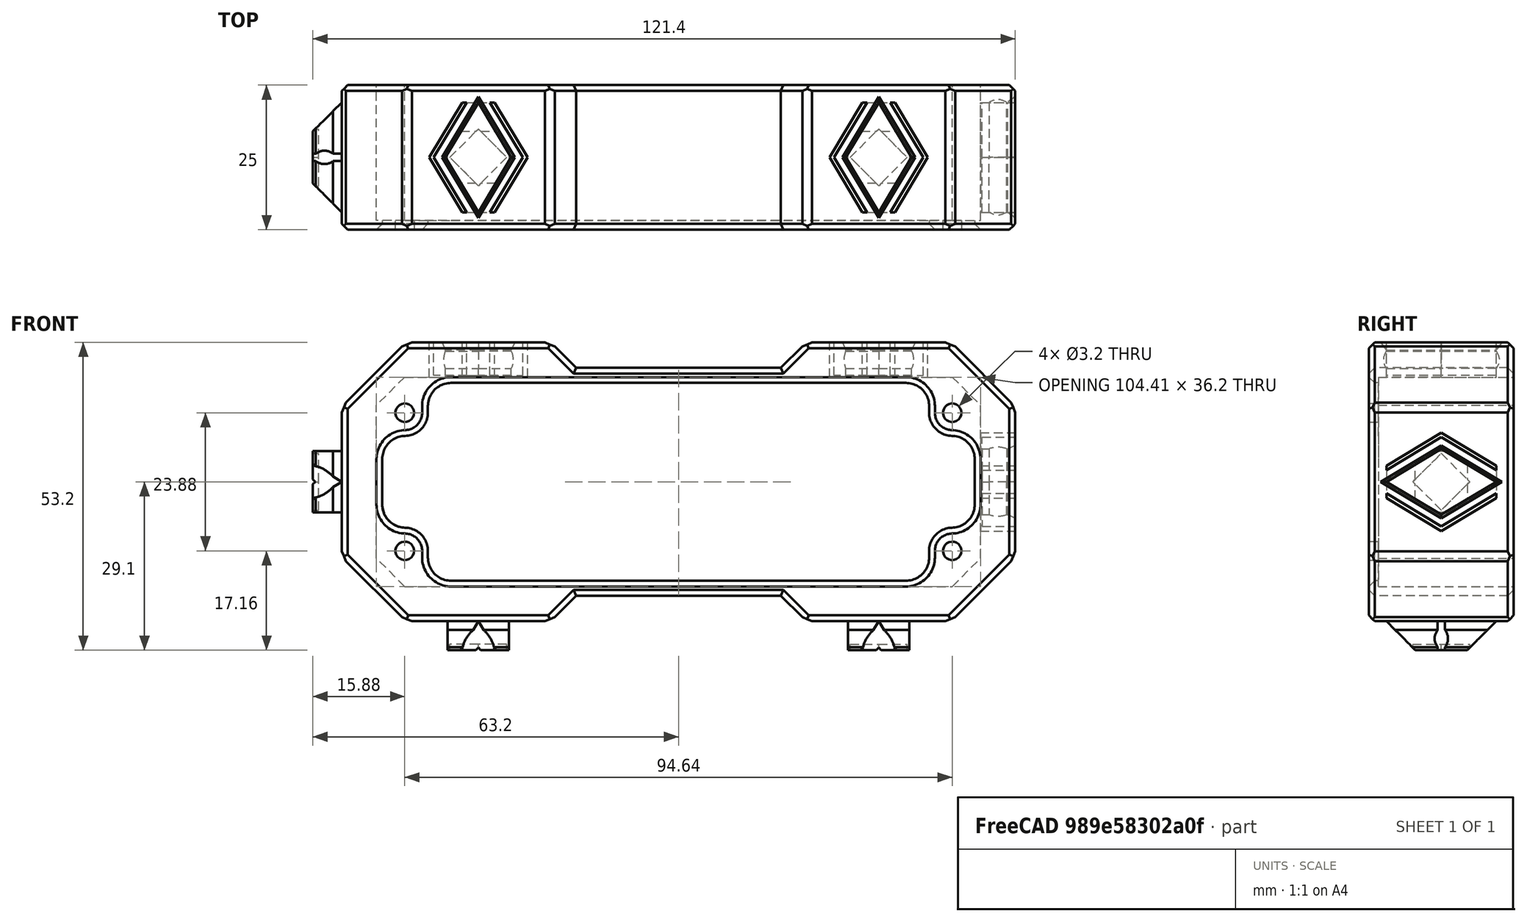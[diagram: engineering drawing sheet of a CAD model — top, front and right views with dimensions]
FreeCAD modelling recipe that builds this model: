
FCSTD DOCUMENT  (FreeCAD 1.1R20251111 (Git shallow))
Label: K93-10436-H7-L120_DockLink_Frame_example
License: All rights reserved
LicenseURL: https://en.wikipedia.org/wiki/All_rights_reserved
objects: App::Link×7, PartDesign::Chamfer×2, Assembly::JointGroup×1, Part::MultiFuse×1, App::Point×1, PartDesign::FeatureBase×1, PartDesign::Body×1
note: 10 computed .brp shape members not serialized (recipe doc carries the construction recipe); baked Part::Feature solids carry a one-line shape summary decoded from their .brp
EXTERNAL_REF file=K93-10436-H7-L120_DockLink_Frame.FCStd obj=Body
EXTERNAL_REF file=../../FreeCAD_DElements/DockLink/DockLink_male.FCStd obj=Body
EXTERNAL_REF file=../../FreeCAD_DElements/DockLink/DockLink_female.FCStd obj=Body

FEATURE [Assembly::JointGroup] Joints
FEATURE [App::Link] K93_10436_H7_L120_DockLink_Frame  label="K93-10436-H7-L120_DockLink_Frame"
  LinkPlacement = pos=(0,-10.9,-10.9) rot=(1,0,0;1.5708rad)
  LinkedObject = -> <external K93-10436-H7-L120_DockLink_Frame.FCStd>#Body
  Placement = pos=(0,-10.9,-10.9) rot=(1,0,0;1.5708rad)
FEATURE [App::Link] Body_DockLink_male
  LinkPlacement = pos=(34.6042,3.94077e-06,-35) rot=(1,0,0;3.14159rad)
  LinkedObject = -> <external ../../FreeCAD_DElements/DockLink/DockLink_male.FCStd>#Body
  Placement = pos=(34.6042,3.94077e-06,-35) rot=(1,0,0;3.14159rad)
FEATURE [App::Link] Body_DockLink_male001
  LinkPlacement = pos=(-34.6042,3.94077e-06,-35) rot=(0,1,0;3.14159rad)
  LinkedObject = -> <external ../../FreeCAD_DElements/DockLink/DockLink_male.FCStd>#Body
  Placement = pos=(-34.6042,3.94077e-06,-35) rot=(0,1,0;3.14159rad)
FEATURE [App::Link] Body_DockLink_male002
  LinkPlacement = pos=(-58.2042,-1.22189e-07,-10.9) rot=(0,1,0;4.71239rad)
  LinkedObject = -> <external ../../FreeCAD_DElements/DockLink/DockLink_male.FCStd>#Body
  Placement = pos=(-58.2042,-1.22189e-07,-10.9) rot=(0,1,0;4.71239rad)
FEATURE [App::Link] Body_DockLink_female
  LinkPlacement = pos=(34.6042,-3.17362e-06,7.2) rot=(1,0,0;0rad)
  LinkedObject = -> <external ../../FreeCAD_DElements/DockLink/DockLink_female.FCStd>#Body
  Placement = pos=(34.6042,-3.17362e-06,7.2) rot=(1,0,0;0rad)
FEATURE [App::Link] Body_DockLink_female002
  LinkPlacement = pos=(-34.6042,-3.17362e-06,7.2) rot=(1,0,0;0rad)
  LinkedObject = -> <external ../../FreeCAD_DElements/DockLink/DockLink_female.FCStd>#Body
  Placement = pos=(-34.6042,-3.17362e-06,7.2) rot=(1,0,0;0rad)
FEATURE [App::Link] Body_DockLink_female003
  LinkPlacement = pos=(52.2042,-1.22189e-07,-10.9) rot=(0,1,0;1.5708rad)
  LinkedObject = -> <external ../../FreeCAD_DElements/DockLink/DockLink_female.FCStd>#Body
  Placement = pos=(52.2042,-1.22189e-07,-10.9) rot=(0,1,0;1.5708rad)
FEATURE [Part::MultiFuse] Fusion
  Refine = true
  Shapes = -> [K93_10436_H7_L120_DockLink_Frame,Body_DockLink_male,Body_DockLink_male001,Body_DockLink_male002,Body_DockLink_female,Body_DockLink_female002,Body_DockLink_female003]
FEATURE [App::Point] Origin005  label="Origin006"
  Role = Origin
FEATURE [PartDesign::FeatureBase] BaseFeature
  BaseFeature = -> Fusion
  Suppressed = false
FEATURE [PartDesign::Chamfer] Chamfer
  Angle = 45
  Base = -> BaseFeature [Edge186,Edge341,Edge191,Edge207,Edge211,Edge212,Edge219,Edge234,Edge349,Edge348,Edge347,Edge346,Edge345,Edge344,Edge343,Edge342,Edge236,Edge221,Edge214,Edge210,Edge206,Edge193,Edge184,Edge494,Edge376,Edge367,Edge356,Edge354,Edge350,Edge357,Edge365,Edge493,Edge49]
  BaseFeature = -> BaseFeature
  ChamferType = 0
  FlipDirection = false
  Refine = true
  Size = 1
  Size2 = 1
  SupportTransform = false
  Suppressed = false
  UseAllEdges = false
FEATURE [PartDesign::Chamfer] Chamfer001
  Angle = 45
  Base = -> Chamfer [Edge285,Edge289,Edge321,Edge325,Edge287,Edge337,Edge341,Edge351,Edge338,Edge312,Edge308,Edge299]
  BaseFeature = -> Chamfer
  ChamferType = 0
  FlipDirection = false
  Refine = true
  Size = 1
  Size2 = 1
  SupportTransform = false
  Suppressed = false
  UseAllEdges = false
FEATURE [PartDesign::Body] Body
  AllowCompound = true
  BaseFeature = -> Fusion
  Group = -> [BaseFeature,Chamfer,Chamfer001]
  Origin = -> Origin004
  Tip = -> Chamfer001

RESOLVED EXTERNAL PARTS (link-assembly join: the EXTERNAL_REF files above that resolve inside this repo's crawl, each included once):
---- part K93-10436-H7-L120_DockLink_Frame.FCStd = doc fcstd_11a9cadb3d35 ----
FCSTD DOCUMENT  (FreeCAD 1.1R20251111 (Git shallow))
Label: K93-10436-H7-L120_DockLink_Frame
License: All rights reserved
LicenseURL: https://en.wikipedia.org/wiki/All_rights_reserved
objects: Sketcher::SketchObject×6, PartDesign::Pocket×4, App::FeaturePython×3, Part::Feature×3, PartDesign::Pad×2, PartDesign::Mirrored×2, App::Point×1, App::DocumentObjectGroupPython×1, App::VarSet×1, PartDesign::Fillet×1, PartDesign::Body×1
note: 41 computed .brp shape members not serialized (recipe doc carries the construction recipe); baked Part::Feature solids carry a one-line shape summary decoded from their .brp

FEATURE [App::Point] Origin001
  Role = Origin
FEATURE [App::FeaturePython] Layer  label="0"  # WARN: FeaturePython — macro-defined, semantics opaque (R4)
FEATURE [App::FeaturePython] Layer001  label="none"  # WARN: FeaturePython — macro-defined, semantics opaque (R4)
FEATURE [App::FeaturePython] Layer002  label="Shape2DView"  # WARN: FeaturePython — macro-defined, semantics opaque (R4)
FEATURE [App::DocumentObjectGroupPython] LayerContainer  label="Layers"  # scripted group (container) (typed FeaturePython)
  Group = -> [Layer,Layer002,Layer001]
FEATURE [Part::Feature] Wire
  shape: bbox 3.2 x 3.2 x 2e-07 mm, 0 faces, 0 solids (baked)
FEATURE [Part::Feature] Wire001
  shape: bbox 3.2 x 3.2 x 2e-07 mm, 0 faces, 0 solids (baked)
FEATURE [Part::Feature] Wire002
  shape: bbox 98.17 x 35.99 x 2e-07 mm, 0 faces, 0 solids (baked)
FEATURE [App::VarSet] VarSet
  depth_feet = 26
  gap = 0.1
  thickness_wall = 1.6
FEATURE [Sketcher::SketchObject] Sketch  label="panel_reference"
  ArcFitTolerance = 1e-06
  ExternalTypes = [0]
  FullyConstrained = true
  MakeInternals = false
  expr: Constraints[35] = VarSet.gap
  expr: Constraints[46] = VarSet.thickness_wall
  expr: Constraints[49] = VarSet.gap * 3
  expr: Constraints[50] = VarSet.gap * 2
  sketch-geometry (16):
    g0: LineSegment [constr] StartX=52.0042 StartY=0 StartZ=0 EndX=52.0042 EndY=12.17 EndZ=0
    g1: ArcOfCircle [constr] CenterX=50.0143 CenterY=12.1873 CenterZ=0 NormalX=0 NormalY=0 NormalZ=1 AngleXU=0 Radius=1.99 StartAngle=6.27451 EndAngle=7.06367
    g2: LineSegment [constr] StartX=51.4283 StartY=13.5875 StartZ=0 EndX=47.5958 EndY=17.42 EndZ=0
    g3: ArcOfCircle [constr] CenterX=46.1874 CenterY=16 CenterZ=0 NormalX=0 NormalY=0 NormalZ=1 AngleXU=0 Radius=2 StartAngle=0.789489 EndAngle=1.57449
    g4: LineSegment [constr] StartX=46.18 StartY=18 StartZ=0 EndX=0 EndY=18 EndZ=0
    g5: Circle [constr] CenterX=47.32 CenterY=11.94 CenterZ=0 NormalX=0 NormalY=0 NormalZ=1 AngleXU=0 Radius=1.61
    g6: LineSegment StartX=52.2042 StartY=0 StartZ=0 EndX=58.2042 EndY=0 EndZ=0
    g7: LineSegment StartX=52.2042 StartY=0 StartZ=0 EndX=52.2042 EndY=13.2359 EndZ=0
    g8: LineSegment StartX=58.2042 StartY=0 StartZ=0 EndX=58.2042 EndY=13 EndZ=0
    g9: LineSegment StartX=47.3401 StartY=18.1 StartZ=0 EndX=52.2042 EndY=13.2359 EndZ=0
    g10: LineSegment StartX=47.1042 StartY=24.1 StartZ=0 EndX=58.2042 EndY=13 EndZ=0
    g11: LineSegment StartX=17.7042 StartY=19.7 StartZ=0 EndX=22.1042 EndY=24.1 EndZ=0
    g12: LineSegment StartX=22.1042 StartY=24.1 StartZ=0 EndX=47.1042 EndY=24.1 EndZ=0
    g13: LineSegment StartX=47.3401 StartY=18.1 StartZ=0 EndX=0 EndY=18.1 EndZ=0
    g14: LineSegment StartX=17.7042 StartY=19.7 StartZ=0 EndX=0 EndY=19.7 EndZ=0
    g15: LineSegment StartX=0 StartY=19.7 StartZ=0 EndX=0 EndY=18.1 EndZ=0
  constraints (52):
    c: Coincident(g3,g4)
    c: Coincident(g2,g3)
    c: Coincident(g1,g2)
    c: Coincident(g0,g1)
    c: PointOnObject(g4,g-2)
    c: Horizontal(g4)
    c: PointOnObject(g6,g-1)
    c: PointOnObject(g6,g-1)
    c: Distance(g4,g-1) = 18
    c: Vertical(g0)
    c: DistanceY(g-1,g0) = 12.17
    c: Distance(g1,g0) = 1.53
    c: Angle(g2,g0) = 2.35619
    c: Distance(g2,g2) = 5.42
    c: Distance(g3,g2) = 1.53
    c: DistanceX(g4,g4) = 46.18
    c: DistanceY(g-1,g2) = 17.42
    c: DistanceY(g-1,g5) = 11.94
    c: Diameter(g5) = 3.22
    c: DistanceX(g-1,g5) = 47.32
    c: Radius(g3) = 2
    c: Radius(g1) = 1.99
    c: PointOnObject(g0,g-1)
    c: Coincident(g7,g6)
    c: Vertical(g7)
    c: Coincident(g8,g6)
    c: Vertical(g8)
    c: Parallel(g2,g9)
    c: Parallel(g9,g10)
    c: Coincident(g9,g7)
    c: Coincident(g10,g8)
    c: Coincident(g12,g11)
    c: Horizontal(g12)
    c: Distance(g9,g12) = 6
    c: Coincident(g10,g12)
    c: Distance(g9,g4) = 0.1
    c: DistanceX(g12,g12) = 25
    c: Coincident(g13,g9)
    c: PointOnObject(g13,g-2)
    c: Horizontal(g13)
    c: Coincident(g14,g11)
    c: PointOnObject(g14,g-2)
    c: Horizontal(g14)
    c: Coincident(g15,g14)
    c: Coincident(g15,g13)
    c: Angle(g11,g14) = 2.35619
    c: DistanceY(g15,g15) = 1.6
    c: Distance(g6,g6) = 6
    c: DistanceY(g8,g8) = 13
    c: Distance(g9,g2) = 0.3
    c: Distance(g0,g7) = 0.2
    c: Distance(g9,g10) = 4.07586
FEATURE [PartDesign::Pad] Pad
  Direction = (0,0,1)
  Length = 23.4
  Length2 = 10
  Profile = -> Sketch
  ReferenceAxis = -> Sketch [N_Axis]
  Refine = true
  Reversed = true
  SideType = 0
  Suppressed = false
  Type = 0
  Type2 = 0
FEATURE [PartDesign::Mirrored] Mirrored
  BaseFeature = -> Pad
  MirrorPlane = -> YZ_Plane
  Refine = true
  Suppressed = false
  TransformMode = 1
FEATURE [PartDesign::Mirrored] Mirrored001
  BaseFeature = -> Mirrored
  MirrorPlane = -> XZ_Plane
  Refine = true
  Suppressed = false
  TransformMode = 1
FEATURE [Sketcher::SketchObject] Sketch001  label="Sketch_Frontplate"
  ArcFitTolerance = 1e-06
  AttachmentSupport = -> [Mirrored001]
  ExternalGeometry = -> [Mirrored001]
  ExternalTypes = [0,0,0,0,0,0,0,0,0,0,0,0,0,0,0,0]
  FullyConstrained = true
  MakeInternals = false
  MapMode = 5
  Placement = pos=(0,0,-7.9e-15) rot=(0,0,1;0rad)
  sketch-geometry (25):
    g0: LineSegment [constr] StartX=-47.32 StartY=11.94 StartZ=0 EndX=-47.32 EndY=-11.94 EndZ=0
    g1: LineSegment [constr] StartX=-47.32 StartY=-11.94 StartZ=0 EndX=47.32 EndY=-11.94 EndZ=0
    g2: LineSegment [constr] StartX=47.32 StartY=-11.94 StartZ=0 EndX=47.32 EndY=11.94 EndZ=0
    g3: LineSegment [constr] StartX=47.32 StartY=11.94 StartZ=0 EndX=-47.32 EndY=11.94 EndZ=0
    g4: GeomPoint [constr] X=0 Y=0 Z=0
    g5: Circle CenterX=-47.32 CenterY=11.94 CenterZ=0 NormalX=0 NormalY=0 NormalZ=1 AngleXU=0 Radius=1.6
    g6: Circle CenterX=-47.32 CenterY=-11.94 CenterZ=0 NormalX=0 NormalY=0 NormalZ=1 AngleXU=0 Radius=1.6
    g7: Circle CenterX=47.32 CenterY=11.94 CenterZ=0 NormalX=0 NormalY=0 NormalZ=1 AngleXU=0 Radius=1.6
    g8: Circle CenterX=47.32 CenterY=-11.94 CenterZ=0 NormalX=0 NormalY=0 NormalZ=1 AngleXU=0 Radius=1.6
    g9: LineSegment StartX=-43.32 StartY=17.1 StartZ=0 EndX=43.32 EndY=17.1 EndZ=0
    g10: LineSegment StartX=-51.2042 StartY=7.94 StartZ=0 EndX=-51.2042 EndY=-7.94 EndZ=0
    g11: LineSegment StartX=51.2042 StartY=7.94 StartZ=0 EndX=51.2042 EndY=-7.94 EndZ=0
    g12: LineSegment StartX=-43.32 StartY=-17.1 StartZ=0 EndX=43.32 EndY=-17.1 EndZ=0
    g13: ArcOfCircle CenterX=-47.32 CenterY=11.94 CenterZ=0 NormalX=0 NormalY=0 NormalZ=1 AngleXU=0 Radius=4 StartAngle=4.71239 EndAngle=6.28319
    g14: ArcOfCircle CenterX=-47.32 CenterY=-11.94 CenterZ=0 NormalX=0 NormalY=0 NormalZ=1 AngleXU=0 Radius=4 StartAngle=0 EndAngle=1.5708
    g15: ArcOfCircle CenterX=47.32 CenterY=-11.94 CenterZ=0 NormalX=0 NormalY=0 NormalZ=1 AngleXU=0 Radius=4 StartAngle=1.5708 EndAngle=3.14159
    g16: ArcOfCircle CenterX=47.32 CenterY=11.94 CenterZ=0 NormalX=0 NormalY=0 NormalZ=1 AngleXU=0 Radius=4 StartAngle=3.14159 EndAngle=4.71239
    g17: LineSegment StartX=43.32 StartY=11.94 StartZ=0 EndX=43.32 EndY=17.1 EndZ=0
    g18: LineSegment StartX=-43.32 StartY=11.94 StartZ=0 EndX=-43.32 EndY=17.1 EndZ=0
    g19: LineSegment StartX=-47.32 StartY=7.94 StartZ=0 EndX=-51.2042 EndY=7.94 EndZ=0
    g20: LineSegment StartX=-47.32 StartY=-7.94 StartZ=0 EndX=-51.2042 EndY=-7.94 EndZ=0
    g21: LineSegment StartX=-43.32 StartY=-17.1 StartZ=0 EndX=-43.32 EndY=-11.94 EndZ=0
    g22: LineSegment StartX=47.32 StartY=7.94 StartZ=0 EndX=51.2042 EndY=7.94 EndZ=0
    g23: LineSegment StartX=47.32 StartY=-7.94 StartZ=0 EndX=51.2042 EndY=-7.94 EndZ=0
    g24: LineSegment StartX=43.32 StartY=-11.94 StartZ=0 EndX=43.32 EndY=-17.1 EndZ=0
  constraints (66):
    c: Coincident(g0,g1)
    c: Coincident(g1,g2)
    c: Coincident(g2,g3)
    c: Coincident(g3,g0)
    c: Vertical(g0)
    c: Vertical(g2)
    c: Horizontal(g1)
    c: Horizontal(g3)
    c: Symmetric(g2,g0,g4)
    c: Coincident(g4,g-1)
    c: Distance(g3,g-1) = 11.94
    c: Distance(g-2,g2) = 47.32
    c: Coincident(g5,g3)
    c: Coincident(g6,g0)
    c: Coincident(g7,g2)
    c: Coincident(g8,g1)
    c: Equal(g8,g7)
    c: Equal(g7,g6)
    c: Equal(g6,g5)
    c: Diameter(g5) = 3.2
    c: Vertical(g10)
    c: Vertical(g11)
    c: Symmetric(g9,g9,g-2)
    c: Symmetric(g12,g12,g-2)
    c: Coincident(g13,g3)
    c: PointOnObject(g13,g0)
    c: PointOnObject(g13,g3)
    c: Radius(g13) = 4
    c: Coincident(g14,g0)
    c: PointOnObject(g14,g0)
    c: PointOnObject(g14,g1)
    c: Coincident(g15,g1)
    c: PointOnObject(g15,g1)
    c: PointOnObject(g15,g2)
    c: Coincident(g16,g2)
    c: PointOnObject(g16,g2)
    c: PointOnObject(g16,g3)
    c: Coincident(g17,g16)
    c: PointOnObject(g17,g9)
    c: Vertical(g17)
    c: Vertical(g9,g17)
    c: Equal(g16,g15)
    c: Equal(g15,g14)
    c: Tangent(g18,g13) = -1.5708
    c: Coincident(g18,g9)
    c: Coincident(g19,g13)
    c: Coincident(g19,g10)
    c: Coincident(g20,g14)
    c: Coincident(g20,g10)
    c: Coincident(g21,g12)
    c: Coincident(g21,g14)
    c: Coincident(g22,g16)
    c: Coincident(g22,g11)
    c: Coincident(g23,g15)
    c: Coincident(g23,g11)
    c: Coincident(g24,g15)
    c: Coincident(g24,g12)
    c: Vertical(g24)
    c: Horizontal(g22)
    c: Horizontal(g23)
    c: Horizontal(g19)
    c: Horizontal(g20)
    c: Distance(g10,g-18) = 7
    c: Distance(g-6,g9) = 2.6
    c: Distance(g-14,g12) = 2.6
    c: Distance(g-10,g11) = 7
FEATURE [PartDesign::Pad] Pad001
  BaseFeature = -> Mirrored001
  Direction = (0,0,1)
  Length = 1.6
  Length2 = 10
  Profile = -> Sketch001
  ReferenceAxis = -> Sketch001 [N_Axis]
  Refine = true
  SideType = 0
  Suppressed = false
  Type = 0
  Type2 = 0
FEATURE [PartDesign::Fillet] Fillet
  Base = -> Pad001 [Edge112,Edge99,Edge100,Edge103,Edge104,Edge107,Edge108,Edge111]
  BaseFeature = -> Pad001
  Radius = 4
  Refine = true
  SupportTransform = false
  Suppressed = false
  UseAllEdges = false
FEATURE [Sketcher::SketchObject] Sketch002
  ArcFitTolerance = 1e-06
  AttachmentSupport = -> [Fillet]
  ExternalGeometry = -> [Fillet]
  ExternalTypes = [0,0]
  FullyConstrained = true
  MakeInternals = false
  MapMode = 5
  Placement = pos=(6.8e-15,24.1,0) rot=(0,0.707107,0.707107;3.14159rad)
FEATURE [PartDesign::Pocket] Pocket
  BaseFeature = -> Fillet
  Direction = (0,-1,2e-16)
  Length = 6
  Length2 = 5
  Profile = -> Sketch002
  ReferenceAxis = -> Sketch002 [N_Axis]
  Refine = true
  SideType = 0
  Suppressed = false
  Type = 0
  Type2 = 0
FEATURE [Sketcher::SketchObject] Sketch003
  ArcFitTolerance = 1e-06
  AttachmentSupport = -> [Pocket]
  ExternalGeometry = -> [Pocket]
  ExternalTypes = [0,0]
  FullyConstrained = true
  MakeInternals = false
  MapMode = 5
  Placement = pos=(6.8e-15,-24.1,-1.06e-14) rot=(1,0,0;1.5708rad)
FEATURE [PartDesign::Pocket] Pocket001
  BaseFeature = -> Pocket
  Direction = (0,1,-2e-16)
  Length = 6
  Length2 = 5
  Profile = -> Sketch003
  ReferenceAxis = -> Sketch003 [N_Axis]
  Refine = true
  SideType = 0
  Suppressed = false
  Type = 0
  Type2 = 0
FEATURE [Sketcher::SketchObject] Sketch004
  ArcFitTolerance = 1e-06
  AttachmentSupport = -> [Pocket001]
  ExternalGeometry = -> [Pocket001]
  ExternalTypes = [0,0,0,0]
  FullyConstrained = true
  MakeInternals = false
  MapMode = 5
  Placement = pos=(-58.2042,0,-1.7e-14) rot=(0.57735,-0.57735,-0.57735;2.0944rad)
  sketch-geometry (8):
    g0: LineSegment [constr] StartX=-13 StartY=1.6 StartZ=0 EndX=13 EndY=-23.4 EndZ=0
    g1: LineSegment [constr] StartX=13 StartY=1.6 StartZ=0 EndX=-13 EndY=-23.4 EndZ=0
    g2: GeomPoint [constr] X=0 Y=-10.9 Z=0
    g3: LineSegment StartX=-12.5 StartY=1.6 StartZ=0 EndX=-12.5 EndY=-23.4 EndZ=0
    g4: LineSegment StartX=-12.5 StartY=-23.4 StartZ=0 EndX=12.5 EndY=-23.4 EndZ=0
    g5: LineSegment StartX=12.5 StartY=-23.4 StartZ=0 EndX=12.5 EndY=1.6 EndZ=0
    g6: LineSegment StartX=12.5 StartY=1.6 StartZ=0 EndX=-12.5 EndY=1.6 EndZ=0
    g7: GeomPoint [constr] X=0 Y=-10.9 Z=0
  constraints (17):
    c: Coincident(g0,g-3)
    c: Coincident(g0,g-6)
    c: Coincident(g1,g-4)
    c: Coincident(g1,g-5)
    c: Symmetric(g1,g1,g2)
    c: Coincident(g3,g4)
    c: Coincident(g4,g5)
    c: Coincident(g5,g6)
    c: Coincident(g6,g3)
    c: Vertical(g3)
    c: Vertical(g5)
    c: Horizontal(g4)
    c: Horizontal(g6)
    c: Symmetric(g5,g3,g7)
    c: Coincident(g7,g2)
    c: Equal(g5,g6)
    c: DistanceX(g6,g6) = 25
FEATURE [PartDesign::Pocket] Pocket002
  BaseFeature = -> Pocket001
  Direction = (1,0,0)
  Length = 6
  Length2 = 5
  Profile = -> Sketch004
  ReferenceAxis = -> Sketch004 [N_Axis]
  Refine = true
  SideType = 0
  Suppressed = false
  Type = 0
  Type2 = 0
FEATURE [Sketcher::SketchObject] Sketch005
  ArcFitTolerance = 1e-06
  AttachmentSupport = -> [Pocket002]
  ExternalGeometry = -> [Pocket002]
  ExternalTypes = [0,0,0,0]
  FullyConstrained = true
  MakeInternals = false
  MapMode = 5
  Placement = pos=(58.2042,0,0) rot=(0.57735,0.57735,0.57735;2.0944rad)
  sketch-geometry (8):
    g0: LineSegment [constr] StartX=-13 StartY=-23.4 StartZ=0 EndX=13 EndY=1.6 EndZ=0
    g1: LineSegment [constr] StartX=13 StartY=-23.4 StartZ=0 EndX=-13 EndY=1.6 EndZ=0
    g2: GeomPoint [constr] X=3e-16 Y=-10.9 Z=0
    g3: LineSegment StartX=-12.5 StartY=1.6 StartZ=0 EndX=-12.5 EndY=-23.4 EndZ=0
    g4: LineSegment StartX=-12.5 StartY=-23.4 StartZ=0 EndX=12.5 EndY=-23.4 EndZ=0
    g5: LineSegment StartX=12.5 StartY=-23.4 StartZ=0 EndX=12.5 EndY=1.6 EndZ=0
    g6: LineSegment StartX=12.5 StartY=1.6 StartZ=0 EndX=-12.5 EndY=1.6 EndZ=0
    g7: GeomPoint [constr] X=3e-16 Y=-10.9 Z=0
  constraints (17):
    c: Coincident(g0,g-6)
    c: Coincident(g0,g-5)
    c: Coincident(g1,g-4)
    c: Coincident(g1,g-3)
    c: Symmetric(g1,g1,g2)
    c: Coincident(g3,g4)
    c: Coincident(g4,g5)
    c: Coincident(g5,g6)
    c: Coincident(g6,g3)
    c: Vertical(g3)
    c: Vertical(g5)
    c: Horizontal(g4)
    c: Horizontal(g6)
    c: Symmetric(g5,g3,g7)
    c: Coincident(g7,g2)
    c: Equal(g5,g6)
    c: DistanceX(g6,g6) = 25
FEATURE [PartDesign::Pocket] Pocket003
  BaseFeature = -> Pocket002
  Direction = (-1,0,0)
  Length = 6
  Length2 = 5
  Profile = -> Sketch005
  ReferenceAxis = -> Sketch005 [N_Axis]
  Refine = true
  SideType = 0
  Suppressed = false
  Type = 0
  Type2 = 0
FEATURE [PartDesign::Body] Body  label="K93-10436-H7-L120_DockLink_Frame"
  AllowCompound = true
  Group = -> [Sketch,Pad,Mirrored,Mirrored001,Sketch001,Pad001,Fillet,Sketch002,Pocket,Sketch003,Pocket001,Sketch004,Pocket002,Sketch005,Pocket003]
  Origin = -> Origin
  Tip = -> Pocket003
